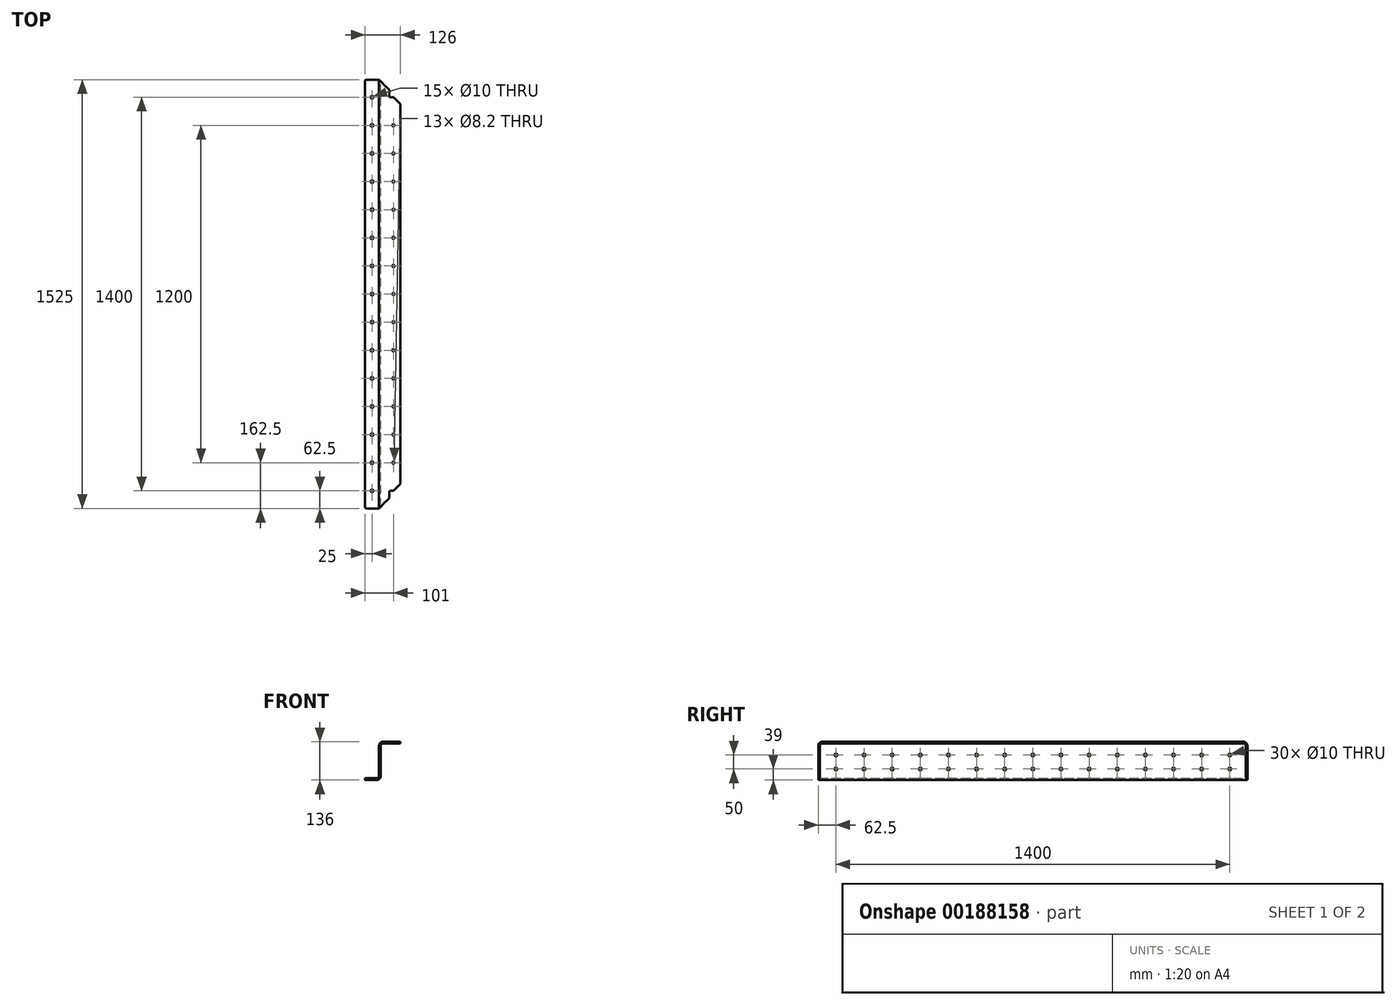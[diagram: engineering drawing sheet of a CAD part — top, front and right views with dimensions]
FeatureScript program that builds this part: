
annotation { "Feature Type Name" : "Feature", "Feature Type Description" : "" }
export const myFeature = defineFeature(function(context is Context, id is Id, definition is map)
    precondition{}
    {
        {
            var Q0;
            Q0=qCreatedBy(makeId("Front.planeOp"),FACE);
            var sketch = newSketch(context, id + "F0", { "sketchPlane" : qUnion([Q0])});
            skLineSegment(sketch, "E0", {"start": v(0, 0) * mm, "end": v(-50, 0) * mm});
            skLineSegment(sketch, "E1", {"start": v(0, 0) * mm, "end": v(0, 130) * mm});
            skLineSegment(sketch, "E2", {"start": v(0, 130) * mm, "end": v(76, 130) * mm});
            skLineSegment(sketch, "E3", {"start": v(76, 130) * mm, "end": v(76, 124) * mm});
            skLineSegment(sketch, "E4", {"start": v(76, 124) * mm, "end": v(6, 124) * mm});
            skLineSegment(sketch, "E5", {"start": v(6, 124) * mm, "end": v(6, -6) * mm});
            skLineSegment(sketch, "E6", {"start": v(6, -6) * mm, "end": v(-50, -6) * mm});
            skLineSegment(sketch, "E7", {"start": v(-50, -6) * mm, "end": v(-50, 0) * mm});
            skSolve(sketch);
        }
        {
            var Q0;
            Q0 = qSketchRegion(id + "F0", true);
            extrude(context, id + "F1", {"entities" : qUnion([Q0]), "depth" : 1525 * mm});
        }
        {
            var Q0;
            Q0=makeQuery(id+"F1.opExtrude","SWEPT_FACE",FACE,{"disambiguationData":[OSD([sQuery(id+"F0.wireOp",EDGE,"E2")])]});
            var sketch = newSketch(context, id + "F2", { "sketchPlane" : qUnion([Q0])});
            skLineSegment(sketch, "E8", {"start": v(76, -762.5) * mm, "end": v(286.6, -762.5) * mm, "construction": true});
            skPoint(sketch, "E8.endSnap0", {"position": v(0, -762.5) * mm});
            skLineSegment(sketch, "E9", {"start": v(76, 0) * mm, "end": v(76, -76) * mm});
            skLineSegment(sketch, "E10", {"start": v(76, -76) * mm, "end": v(0, 0) * mm});
            skLineSegment(sketch, "E11", {"start": v(0, 0) * mm, "end": v(76, 0) * mm});
            skLineSegment(sketch, "E12.MirrorCS", {"start": v(76, -1449) * mm, "end": v(0, -1525) * mm});
            skLineSegment(sketch, "E13.MirrorCS", {"start": v(76, -1525) * mm, "end": v(76, -1449) * mm});
            skLineSegment(sketch, "E14.MirrorCS", {"start": v(0, -1525) * mm, "end": v(76, -1525) * mm});
            skSolve(sketch);
        }
        {
            var Q0;
            Q0 = qSketchRegion(id + "F2", true);
            extrude(context, id + "F3", {"entities" : qUnion([Q0]), "operationType" : NewBodyOperationType.REMOVE, "endBound" : BoundingType.THROUGH_ALL, "oppositeDirection" : true, "depth" : 25 * mm});
        }
        {
            var Q0;
            Q0=makeQuery(id+"F1.opExtrude","SWEPT_EDGE",EDGE,{"disambiguationData":[OSD([sQuery(id+"F0.wireOp",EDGE,"E4"),sQuery(id+"F0.wireOp",EDGE,"E5")])]});
            fillet(context, id + "F4", {"entities" : qUnion([Q0]), "radius" : 8 * mm, "tangentPropagation" : true, "allowEdgeOverflow" : false});
        }
        {
            var Q0;
            Q0=makeQuery(id+"F1.opExtrude","SWEPT_EDGE",EDGE,{"disambiguationData":[OSD([sQuery(id+"F0.wireOp",EDGE,"E0"),sQuery(id+"F0.wireOp",EDGE,"E1")])]});
            fillet(context, id + "F5", {"entities" : qUnion([Q0]), "radius" : 8 * mm, "tangentPropagation" : true, "allowEdgeOverflow" : false});
        }
        {
            var Q0;
            Q0=makeQuery(id+"F1.opExtrude","SWEPT_EDGE",EDGE,{"disambiguationData":[OSD([sQuery(id+"F0.wireOp",EDGE,"E1"),sQuery(id+"F0.wireOp",EDGE,"E2")])]});
            fillet(context, id + "F6", {"entities" : qUnion([Q0]), "radius" : 14 * mm, "tangentPropagation" : true, "allowEdgeOverflow" : false});
        }
        {
            var Q0;
            Q0=makeQuery(id+"F1.opExtrude","SWEPT_EDGE",EDGE,{"disambiguationData":[OSD([sQuery(id+"F0.wireOp",EDGE,"E5"),sQuery(id+"F0.wireOp",EDGE,"E6")])]});
            fillet(context, id + "F7", {"entities" : qUnion([Q0]), "radius" : 14 * mm, "tangentPropagation" : true, "allowEdgeOverflow" : false});
        }
        {
            var Q0;
            Q0=makeQuery(id+"F1.opExtrude","SWEPT_FACE",FACE,{"disambiguationData":[OSD([sQuery(id+"F0.wireOp",EDGE,"E2")])]});
            var sketch = newSketch(context, id + "F8", { "sketchPlane" : qUnion([Q0])});
            skCircle(sketch, "E15", {"center": v(51, -1362.5) * mm, "radius": 4.1 * mm});
            skCircle(sketch, "E16.0.1.0", {"center": v(51, -1262.5) * mm, "radius": 4.1 * mm});
            skCircle(sketch, "E16.0.2.0", {"center": v(51, -1162.5) * mm, "radius": 4.1 * mm});
            skCircle(sketch, "E16.0.3.0", {"center": v(51, -1062.5) * mm, "radius": 4.1 * mm});
            skCircle(sketch, "E16.0.4.0", {"center": v(51, -962.5) * mm, "radius": 4.1 * mm});
            skCircle(sketch, "E16.0.5.0", {"center": v(51, -862.5) * mm, "radius": 4.1 * mm});
            skCircle(sketch, "E16.0.6.0", {"center": v(51, -762.5) * mm, "radius": 4.1 * mm});
            skCircle(sketch, "E16.0.7.0", {"center": v(51, -662.5) * mm, "radius": 4.1 * mm});
            skCircle(sketch, "E16.0.8.0", {"center": v(51, -562.5) * mm, "radius": 4.1 * mm});
            skCircle(sketch, "E16.0.9.0", {"center": v(51, -462.5) * mm, "radius": 4.1 * mm});
            skLineSegment(sketch, "E16.direction1", {"start": v(51, -1362.5) * mm, "end": v(84.6, -1362.5) * mm, "construction": true});
            skLineSegment(sketch, "E16.direction2", {"start": v(51, -1362.5) * mm, "end": v(51, -1262.5) * mm, "construction": true});
            skLineSegment(sketch, "E17", {"start": v(76, -762.5) * mm, "end": v(14, -762.5) * mm, "construction": true});
            skCircle(sketch, "E18.0.0.10", {"center": v(51, -362.5) * mm, "radius": 4.1 * mm});
            skCircle(sketch, "E18.0.0.11", {"center": v(51, -262.5) * mm, "radius": 4.1 * mm});
            skCircle(sketch, "E18.0.0.12", {"center": v(51, -162.5) * mm, "radius": 4.1 * mm});
            skSolve(sketch);
        }
        {
            var Q0;
            Q0 = qSketchRegion(id + "F8", true);
            extrude(context, id + "F9", {"entities" : qUnion([Q0]), "operationType" : NewBodyOperationType.REMOVE, "endBound" : BoundingType.THROUGH_ALL, "oppositeDirection" : true, "depth" : 25 * mm});
        }
        {
            var Q0;
            Q0=makeQuery(id+"F1.opExtrude","SWEPT_FACE",FACE,{"disambiguationData":[OSD([sQuery(id+"F0.wireOp",EDGE,"E1")])]});
            var sketch = newSketch(context, id + "F10", { "sketchPlane" : qUnion([Q0])});
            skLineSegment(sketch, "E19", {"start": v(1461.99, 33) * mm, "end": v(894.83, 33) * mm, "construction": true});
            skCircle(sketch, "E20", {"center": v(1462.5, 33) * mm, "radius": 5 * mm});
            skCircle(sketch, "E21.1.0.0", {"center": v(1362.5, 33) * mm, "radius": 5 * mm});
            skCircle(sketch, "E21.2.0.0", {"center": v(1262.5, 33) * mm, "radius": 5 * mm});
            skCircle(sketch, "E21.3.0.0", {"center": v(1162.5, 33) * mm, "radius": 5 * mm});
            skCircle(sketch, "E21.4.0.0", {"center": v(1062.5, 33) * mm, "radius": 5 * mm});
            skCircle(sketch, "E21.5.0.0", {"center": v(962.5, 33) * mm, "radius": 5 * mm});
            skCircle(sketch, "E21.6.0.0", {"center": v(862.5, 33) * mm, "radius": 5 * mm});
            skCircle(sketch, "E21.7.0.0", {"center": v(762.5, 33) * mm, "radius": 5 * mm});
            skCircle(sketch, "E21.8.0.0", {"center": v(662.5, 33) * mm, "radius": 5 * mm});
            skCircle(sketch, "E21.9.0.0", {"center": v(562.5, 33) * mm, "radius": 5 * mm});
            skCircle(sketch, "E21.10.0.0", {"center": v(462.5, 33) * mm, "radius": 5 * mm});
            skCircle(sketch, "E21.11.0.0", {"center": v(362.5, 33) * mm, "radius": 5 * mm});
            skCircle(sketch, "E21.12.0.0", {"center": v(262.5, 33) * mm, "radius": 5 * mm});
            skLineSegment(sketch, "E21.direction1", {"start": v(1462.5, 33) * mm, "end": v(1362.5, 33) * mm, "construction": true});
            skLineSegment(sketch, "E22", {"start": v(762.5, 58) * mm, "end": v(762.5, 8) * mm, "construction": true});
            skCircle(sketch, "E23.0.13.0", {"center": v(162.5, 33) * mm, "radius": 5 * mm});
            skCircle(sketch, "E23.0.14.0", {"center": v(62.5, 33) * mm, "radius": 5 * mm});
            skLineSegment(sketch, "E24", {"start": v(1423.58, 58) * mm, "end": v(1192.6, 58) * mm, "construction": true});
            skCircle(sketch, "E25.MirrorC", {"center": v(1462.5, 83) * mm, "radius": 5 * mm});
            skCircle(sketch, "E26.MirrorC", {"center": v(1362.5, 83) * mm, "radius": 5 * mm});
            skCircle(sketch, "E27.MirrorC", {"center": v(1262.5, 83) * mm, "radius": 5 * mm});
            skCircle(sketch, "E28.MirrorC", {"center": v(1162.5, 83) * mm, "radius": 5 * mm});
            skCircle(sketch, "E29.MirrorC", {"center": v(1062.5, 83) * mm, "radius": 5 * mm});
            skCircle(sketch, "E30.MirrorC", {"center": v(962.5, 83) * mm, "radius": 5 * mm});
            skCircle(sketch, "E31.MirrorC", {"center": v(862.5, 83) * mm, "radius": 5 * mm});
            skCircle(sketch, "E32.MirrorC", {"center": v(462.5, 83) * mm, "radius": 5 * mm});
            skCircle(sketch, "E33.MirrorC", {"center": v(562.5, 83) * mm, "radius": 5 * mm});
            skCircle(sketch, "E34.MirrorC", {"center": v(662.5, 83) * mm, "radius": 5 * mm});
            skCircle(sketch, "E35.MirrorC", {"center": v(762.5, 83) * mm, "radius": 5 * mm});
            skCircle(sketch, "E36.MirrorC", {"center": v(162.5, 83) * mm, "radius": 5 * mm});
            skCircle(sketch, "E37.MirrorC", {"center": v(262.5, 83) * mm, "radius": 5 * mm});
            skCircle(sketch, "E38.MirrorC", {"center": v(62.5, 83) * mm, "radius": 5 * mm});
            skCircle(sketch, "E39.MirrorC", {"center": v(362.5, 83) * mm, "radius": 5 * mm});
            skSolve(sketch);
        }
        {
            var Q0;
            Q0 = qSketchRegion(id + "F10", true);
            extrude(context, id + "F11", {"entities" : qUnion([Q0]), "operationType" : NewBodyOperationType.REMOVE, "endBound" : BoundingType.THROUGH_ALL, "oppositeDirection" : true, "depth" : 25 * mm});
        }
        {
            var Q0;
            Q0=makeQuery(id+"F1.opExtrude","SWEPT_FACE",FACE,{"disambiguationData":[OSD([sQuery(id+"F0.wireOp",EDGE,"E0")])]});
            var sketch = newSketch(context, id + "F12", { "sketchPlane" : qUnion([Q0])});
            skLineSegment(sketch, "E40", {"start": v(-25, -1551.82) * mm, "end": v(-25, -1525) * mm, "construction": true});
            skCircle(sketch, "E41", {"center": v(-25, -1462.5) * mm, "radius": 5 * mm});
            skLineSegment(sketch, "E42", {"start": v(-50, -762.5) * mm, "end": v(0, -762.5) * mm, "construction": true});
            skCircle(sketch, "E43.0.1.0", {"center": v(-25, -1362.5) * mm, "radius": 5 * mm});
            skCircle(sketch, "E43.0.2.0", {"center": v(-25, -1262.5) * mm, "radius": 5 * mm});
            skCircle(sketch, "E43.0.3.0", {"center": v(-25, -1162.5) * mm, "radius": 5 * mm});
            skCircle(sketch, "E43.0.4.0", {"center": v(-25, -1062.5) * mm, "radius": 5 * mm});
            skCircle(sketch, "E43.0.5.0", {"center": v(-25, -962.5) * mm, "radius": 5 * mm});
            skCircle(sketch, "E43.0.6.0", {"center": v(-25, -862.5) * mm, "radius": 5 * mm});
            skLineSegment(sketch, "E43.direction1", {"start": v(-25, -1462.5) * mm, "end": v(1.7, -1462.5) * mm, "construction": true});
            skLineSegment(sketch, "E43.direction2", {"start": v(-25, -1462.5) * mm, "end": v(-25, -1362.5) * mm, "construction": true});
            skCircle(sketch, "E44.0.0.7", {"center": v(-25, -762.5) * mm, "radius": 5 * mm});
            skCircle(sketch, "E44.0.0.8", {"center": v(-25, -662.5) * mm, "radius": 5 * mm});
            skCircle(sketch, "E44.0.0.9", {"center": v(-25, -562.5) * mm, "radius": 5 * mm});
            skCircle(sketch, "E44.0.0.10", {"center": v(-25, -462.5) * mm, "radius": 5 * mm});
            skCircle(sketch, "E44.0.0.11", {"center": v(-25, -362.5) * mm, "radius": 5 * mm});
            skCircle(sketch, "E44.0.0.12", {"center": v(-25, -262.5) * mm, "radius": 5 * mm});
            skCircle(sketch, "E44.0.0.13", {"center": v(-25, -162.5) * mm, "radius": 5 * mm});
            skCircle(sketch, "E44.0.0.14", {"center": v(-25, -62.5) * mm, "radius": 5 * mm});
            skSolve(sketch);
        }
        {
            var Q0;
            Q0 = qSketchRegion(id + "F12", true);
            extrude(context, id + "F13", {"entities" : qUnion([Q0]), "operationType" : NewBodyOperationType.REMOVE, "endBound" : BoundingType.THROUGH_ALL, "oppositeDirection" : true, "depth" : 25 * mm});
        }
        {
            var Q0;
            Q0=makeQuery(id+"F1.opExtrude","SWEPT_FACE",FACE,{"disambiguationData":[OSD([sQuery(id+"F0.wireOp",EDGE,"E2")])]});
            var sketch = newSketch(context, id + "F14", { "sketchPlane" : qUnion([Q0])});
            skLineSegment(sketch, "E45", {"start": v(36, -36) * mm, "end": v(36, -62.5) * mm});
            skLineSegment(sketch, "E46", {"start": v(36, -36) * mm, "end": v(76, -76) * mm});
            skLineSegment(sketch, "E47", {"start": v(36, -62.5) * mm, "end": v(51.19, -62.5) * mm});
            skLineSegment(sketch, "E48", {"start": v(76, -762.5) * mm, "end": v(177.14, -762.5) * mm, "construction": true});
            skLineSegment(sketch, "E49.MirrorCS", {"start": v(36, -1489) * mm, "end": v(36, -1462.5) * mm});
            skLineSegment(sketch, "E50.MirrorCS", {"start": v(36, -1489) * mm, "end": v(76, -1449) * mm});
            skLineSegment(sketch, "E51.MirrorCS", {"start": v(36, -1462.5) * mm, "end": v(51.19, -1462.5) * mm});
            skPoint(sketch, "E52", {"position": v(51, -162.5) * mm});
            skLineSegment(sketch, "E53", {"start": v(51.19, -62.5) * mm, "end": v(76, -87.31) * mm});
            skLineSegment(sketch, "E54", {"start": v(76, -87.31) * mm, "end": v(76, -76) * mm});
            skLineSegment(sketch, "E55.MirrorCS", {"start": v(51.19, -1462.5) * mm, "end": v(76, -1437.69) * mm});
            skLineSegment(sketch, "E56.MirrorCS", {"start": v(76, -1437.69) * mm, "end": v(76, -1449) * mm});
            skSolve(sketch);
        }
        {
            var Q0;
            Q0 = qSketchRegion(id + "F14", true);
            extrude(context, id + "F15", {"entities" : qUnion([Q0]), "operationType" : NewBodyOperationType.REMOVE, "endBound" : BoundingType.THROUGH_ALL, "oppositeDirection" : true, "depth" : 25 * mm});
        }
        {
            var Q0;
            Q0=makeQuery(id+"F15.boolean.opBoolean","COPY",EDGE,{"derivedFrom":makeQuery(id+"F15.opExtrude","SWEPT_EDGE",EDGE,{"disambiguationData":[OSD([sQuery(id+"F2.wireOp",EDGE,"E10"),sQuery(id+"F14.wireOp",EDGE,"E45"),sQuery(id+"F14.wireOp",EDGE,"E46")])]})});
            var Q1;
            Q1=makeQuery(id+"F15.boolean.opBoolean","COPY",EDGE,{"derivedFrom":makeQuery(id+"F15.opExtrude","SWEPT_EDGE",EDGE,{"disambiguationData":[OSD([sQuery(id+"F14.wireOp",EDGE,"E45"),sQuery(id+"F14.wireOp",EDGE,"E47")])]})});
            var Q2;
            Q2=makeQuery(id+"F15.boolean.opBoolean","COPY",EDGE,{"derivedFrom":makeQuery(id+"F15.opExtrude","SWEPT_EDGE",EDGE,{"disambiguationData":[OSD([sQuery(id+"F2.wireOp",EDGE,"E10"),sQuery(id+"F14.wireOp",EDGE,"E46"),sQuery(id+"F14.wireOp",EDGE,"E47")])]})});
            var Q3;
            Q3=makeQuery(id+"F15.boolean.opBoolean","COPY",EDGE,{"derivedFrom":makeQuery(id+"F15.opExtrude","SWEPT_EDGE",EDGE,{"disambiguationData":[OSD([sQuery(id+"F2.wireOp",EDGE,"E12.MirrorCS"),sQuery(id+"F14.wireOp",EDGE,"E49.MirrorCS"),sQuery(id+"F14.wireOp",EDGE,"E50.MirrorCS")])]})});
            var Q4;
            Q4=makeQuery(id+"F15.boolean.opBoolean","COPY",EDGE,{"derivedFrom":makeQuery(id+"F15.opExtrude","SWEPT_EDGE",EDGE,{"disambiguationData":[OSD([sQuery(id+"F14.wireOp",EDGE,"E49.MirrorCS"),sQuery(id+"F14.wireOp",EDGE,"E51.MirrorCS")])]})});
            var Q5;
            Q5=makeQuery(id+"F15.boolean.opBoolean","COPY",EDGE,{"derivedFrom":makeQuery(id+"F15.opExtrude","SWEPT_EDGE",EDGE,{"disambiguationData":[OSD([sQuery(id+"F2.wireOp",EDGE,"E12.MirrorCS"),sQuery(id+"F14.wireOp",EDGE,"E50.MirrorCS"),sQuery(id+"F14.wireOp",EDGE,"E51.MirrorCS")])]})});
            var Q6;
            Q6=makeQuery(id+"F15.boolean.opBoolean","COPY",EDGE,{"derivedFrom":makeQuery(id+"F15.opExtrude","SWEPT_EDGE",EDGE,{"disambiguationData":[OSD([sQuery(id+"F14.wireOp",EDGE,"E47"),sQuery(id+"F14.wireOp",EDGE,"E53")])]})});
            var Q7;
            Q7=makeQuery(id+"F15.boolean.opBoolean","COPY",EDGE,{"derivedFrom":makeQuery(id+"F15.opExtrude","SWEPT_EDGE",EDGE,{"disambiguationData":[OSD([sQuery(id+"F0.wireOp",EDGE,"E2"),sQuery(id+"F0.wireOp",EDGE,"E3"),sQuery(id+"F14.wireOp",EDGE,"E53"),sQuery(id+"F14.wireOp",EDGE,"E54")])]})});
            var Q8;
            Q8=makeQuery(id+"F15.boolean.opBoolean","COPY",EDGE,{"derivedFrom":makeQuery(id+"F15.opExtrude","SWEPT_EDGE",EDGE,{"disambiguationData":[OSD([sQuery(id+"F14.wireOp",EDGE,"E51.MirrorCS"),sQuery(id+"F14.wireOp",EDGE,"E55.MirrorCS")])]})});
            var Q9;
            Q9=makeQuery(id+"F15.boolean.opBoolean","COPY",EDGE,{"derivedFrom":makeQuery(id+"F15.opExtrude","SWEPT_EDGE",EDGE,{"disambiguationData":[OSD([sQuery(id+"F0.wireOp",EDGE,"E2"),sQuery(id+"F0.wireOp",EDGE,"E3"),sQuery(id+"F14.wireOp",EDGE,"E55.MirrorCS"),sQuery(id+"F14.wireOp",EDGE,"E56.MirrorCS")])]})});
            fillet(context, id + "F16", {"entities" : qUnion([Q0, Q1, Q2, Q3, Q4, Q5, Q6, Q7, Q8, Q9]), "radius" : 5 * mm, "tangentPropagation" : true, "allowEdgeOverflow" : false});
        }
        {
            var Q0;
            Q0=makeQuery(id+"F1.opExtrude","CAP_EDGE",EDGE,{"disambiguationData":[OSD([sQuery(id+"F0.wireOp",EDGE,"E7")])],"isStart":false});
            var Q1;
            Q1=makeQuery(id+"F3.boolean.opBoolean","COPY",EDGE,{"derivedFrom":makeQuery(id+"F3.opExtrude","SWEPT_EDGE",EDGE,{"disambiguationData":[OSD([sQuery(id+"F0.wireOp",EDGE,"E2"),sQuery(id+"F0.wireOp",EDGE,"E3"),sQuery(id+"F2.wireOp",EDGE,"E12.MirrorCS"),sQuery(id+"F2.wireOp",EDGE,"E13.MirrorCS")])]})});
            var Q2;
            Q2=makeQuery(id+"F3.boolean.opBoolean","COPY",EDGE,{"derivedFrom":makeQuery(id+"F3.opExtrude","SWEPT_EDGE",EDGE,{"disambiguationData":[OSD([sQuery(id+"F0.wireOp",EDGE,"E2"),sQuery(id+"F0.wireOp",EDGE,"E3"),sQuery(id+"F2.wireOp",EDGE,"E9"),sQuery(id+"F2.wireOp",EDGE,"E10")])]})});
            var Q3;
            Q3=makeQuery(id+"F1.opExtrude","CAP_EDGE",EDGE,{"disambiguationData":[OSD([sQuery(id+"F0.wireOp",EDGE,"E7")])],"isStart":true});
            fillet(context, id + "F17", {"entities" : qUnion([Q0, Q1, Q2, Q3]), "radius" : 5 * mm, "tangentPropagation" : true, "allowEdgeOverflow" : false});
        }
    });
